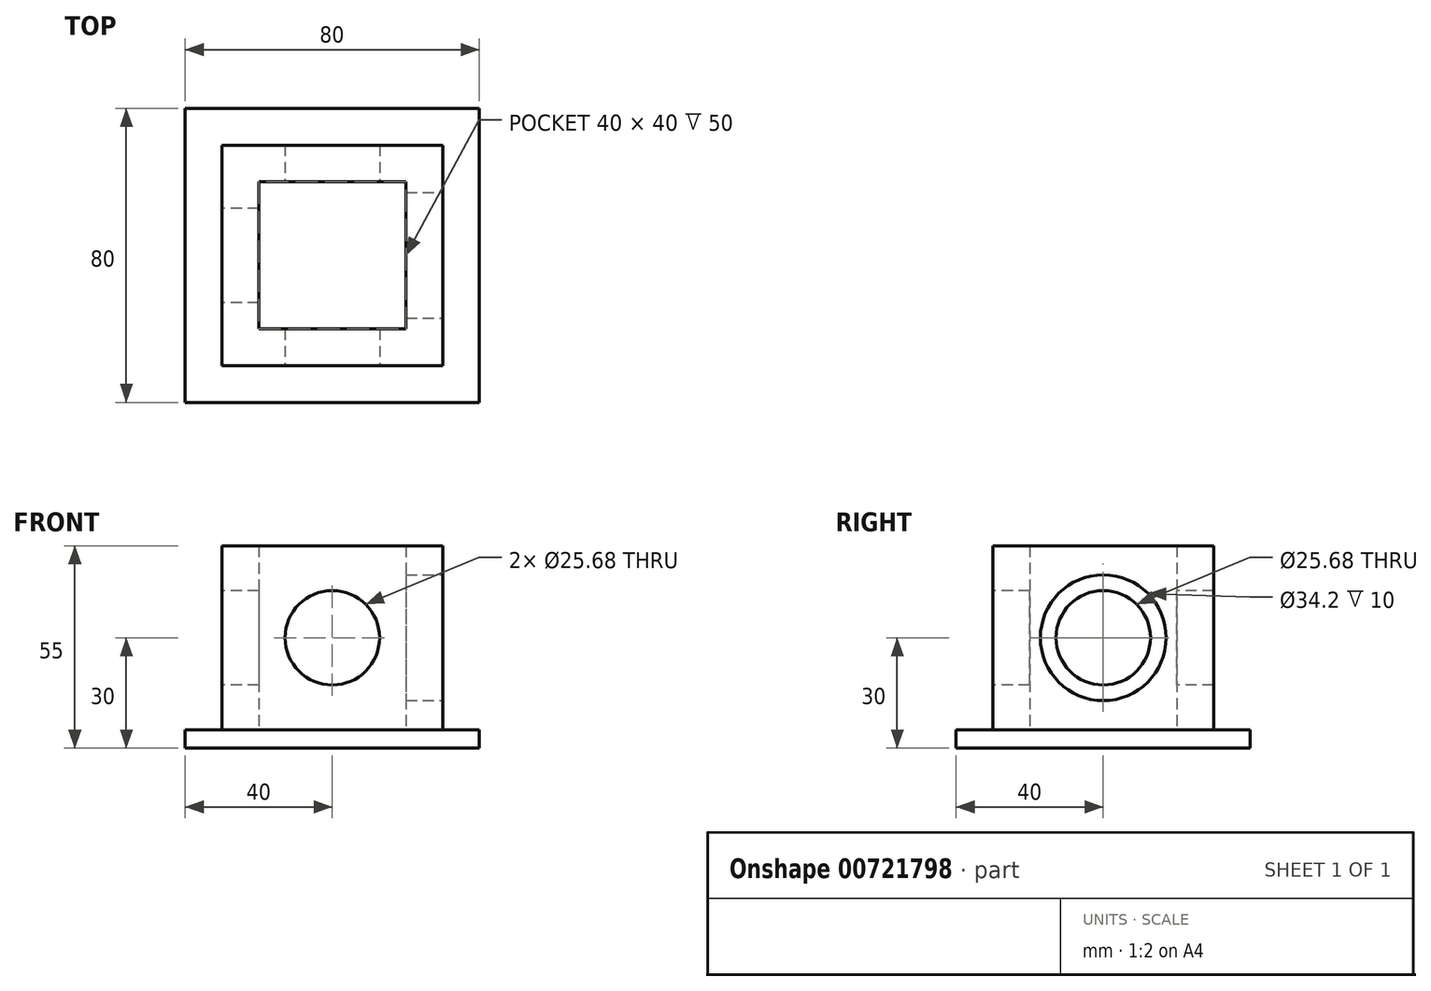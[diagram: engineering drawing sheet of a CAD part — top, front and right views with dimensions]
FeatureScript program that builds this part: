
annotation { "Feature Type Name" : "Feature", "Feature Type Description" : "" }
export const myFeature = defineFeature(function(context is Context, id is Id, definition is map)
    precondition{}
    {
        {
            var Q0;
            Q0=qCreatedBy(makeId("Top.planeOp"),FACE);
            var sketch = newSketch(context, id + "F0", { "sketchPlane" : qUnion([Q0])});
            skLineSegment(sketch, "E0.bottom", {"start": v(30, -30) * mm, "end": v(-30, -30) * mm});
            skLineSegment(sketch, "E0.top", {"start": v(30, 30) * mm, "end": v(-30, 30) * mm});
            skLineSegment(sketch, "E0.left", {"start": v(30, -30) * mm, "end": v(30, 30) * mm});
            skLineSegment(sketch, "E0.right", {"start": v(-30, -30) * mm, "end": v(-30, 30) * mm});
            skPoint(sketch, "E0.middle", {"position": v(0, 0) * mm});
            skSolve(sketch);
        }
        {
            var Q0;
            Q0=qCreatedBy(makeId("Top.planeOp"),FACE);
            var sketch = newSketch(context, id + "F1", { "sketchPlane" : qUnion([Q0])});
            skLineSegment(sketch, "E1.bottom", {"start": v(20, -20) * mm, "end": v(-20, -20) * mm});
            skLineSegment(sketch, "E1.top", {"start": v(20, 20) * mm, "end": v(-20, 20) * mm});
            skLineSegment(sketch, "E1.left", {"start": v(20, -20) * mm, "end": v(20, 20) * mm});
            skLineSegment(sketch, "E1.right", {"start": v(-20, -20) * mm, "end": v(-20, 20) * mm});
            skPoint(sketch, "E1.middle", {"position": v(0, 0) * mm});
            skSolve(sketch);
        }
        {
            var Q0;
            Q0 = qSketchRegion(id + "F0", true);
            extrude(context, id + "F2", {"entities" : qUnion([Q0]), "depth" : 50 * mm, "offsetDistance" : 25 * mm});
        }
        {
            var Q0;
            Q0 = qSketchRegion(id + "F1", true);
            extrude(context, id + "F3", {"entities" : qUnion([Q0]), "operationType" : NewBodyOperationType.REMOVE, "depth" : 50 * mm, "offsetDistance" : 25 * mm});
        }
        {
            var Q0;
            Q0=makeQuery(id+"F2.opExtrude","SWEPT_FACE",FACE,{"disambiguationData":[OSD([sQuery(id+"F0.wireOp",EDGE,"E0.bottom")])]});
            var sketch = newSketch(context, id + "F4", { "sketchPlane" : qUnion([Q0])});
            skCircle(sketch, "E2", {"center": v(0, 25) * mm, "radius": 12.84 * mm});
            skPoint(sketch, "E2.centerSnap0", {"position": v(-30, 25) * mm});
            skSolve(sketch);
        }
        {
            var Q0;
            Q0 = qSketchRegion(id + "F4", true);
            extrude(context, id + "F5", {"entities" : qUnion([Q0]), "operationType" : NewBodyOperationType.REMOVE, "oppositeDirection" : true, "depth" : 60 * mm, "offsetDistance" : 25 * mm});
        }
        {
            var Q0;
            Q0=makeQuery(id+"F2.opExtrude","SWEPT_FACE",FACE,{"disambiguationData":[OSD([sQuery(id+"F0.wireOp",EDGE,"E0.right")])]});
            var sketch = newSketch(context, id + "F6", { "sketchPlane" : qUnion([Q0])});
            skCircle(sketch, "E3", {"center": v(0, 25) * mm, "radius": 12.84 * mm});
            skPoint(sketch, "E3.centerSnap0", {"position": v(30, 25) * mm});
            skSolve(sketch);
        }
        {
            var Q0;
            Q0 = qSketchRegion(id + "F6", true);
            extrude(context, id + "F7", {"entities" : qUnion([Q0]), "operationType" : NewBodyOperationType.REMOVE, "oppositeDirection" : true, "depth" : 10 * mm, "offsetDistance" : 25 * mm});
        }
        {
            var Q0;
            Q0=makeQuery(id+"F2.opExtrude","SWEPT_FACE",FACE,{"disambiguationData":[OSD([sQuery(id+"F0.wireOp",EDGE,"E0.left")])]});
            var sketch = newSketch(context, id + "F8", { "sketchPlane" : qUnion([Q0])});
            skCircle(sketch, "E4", {"center": v(0, 25) * mm, "radius": 17.1 * mm});
            skPoint(sketch, "E4.centerSnap0", {"position": v(30, 25) * mm});
            skSolve(sketch);
        }
        {
            var Q0;
            Q0 = qSketchRegion(id + "F8", true);
            extrude(context, id + "F9", {"entities" : qUnion([Q0]), "operationType" : NewBodyOperationType.REMOVE, "oppositeDirection" : true, "depth" : 25 * mm, "offsetDistance" : 25 * mm});
        }
        {
            var Q0;
            Q0=qCreatedBy(makeId("Top.planeOp"),FACE);
            var sketch = newSketch(context, id + "F10", { "sketchPlane" : qUnion([Q0])});
            skLineSegment(sketch, "E5.bottom", {"start": v(40, 40) * mm, "end": v(-40, 40) * mm});
            skLineSegment(sketch, "E5.top", {"start": v(40, -40) * mm, "end": v(-40, -40) * mm});
            skLineSegment(sketch, "E5.left", {"start": v(40, 40) * mm, "end": v(40, -40) * mm});
            skLineSegment(sketch, "E5.right", {"start": v(-40, 40) * mm, "end": v(-40, -40) * mm});
            skPoint(sketch, "E5.middle", {"position": v(0, 0) * mm});
            skSolve(sketch);
        }
        {
            var Q0;
            Q0 = qSketchRegion(id + "F10", true);
            extrude(context, id + "F11", {"entities" : qUnion([Q0]), "operationType" : NewBodyOperationType.ADD, "oppositeDirection" : true, "depth" : 5 * mm, "offsetDistance" : 25 * mm});
        }
    });
